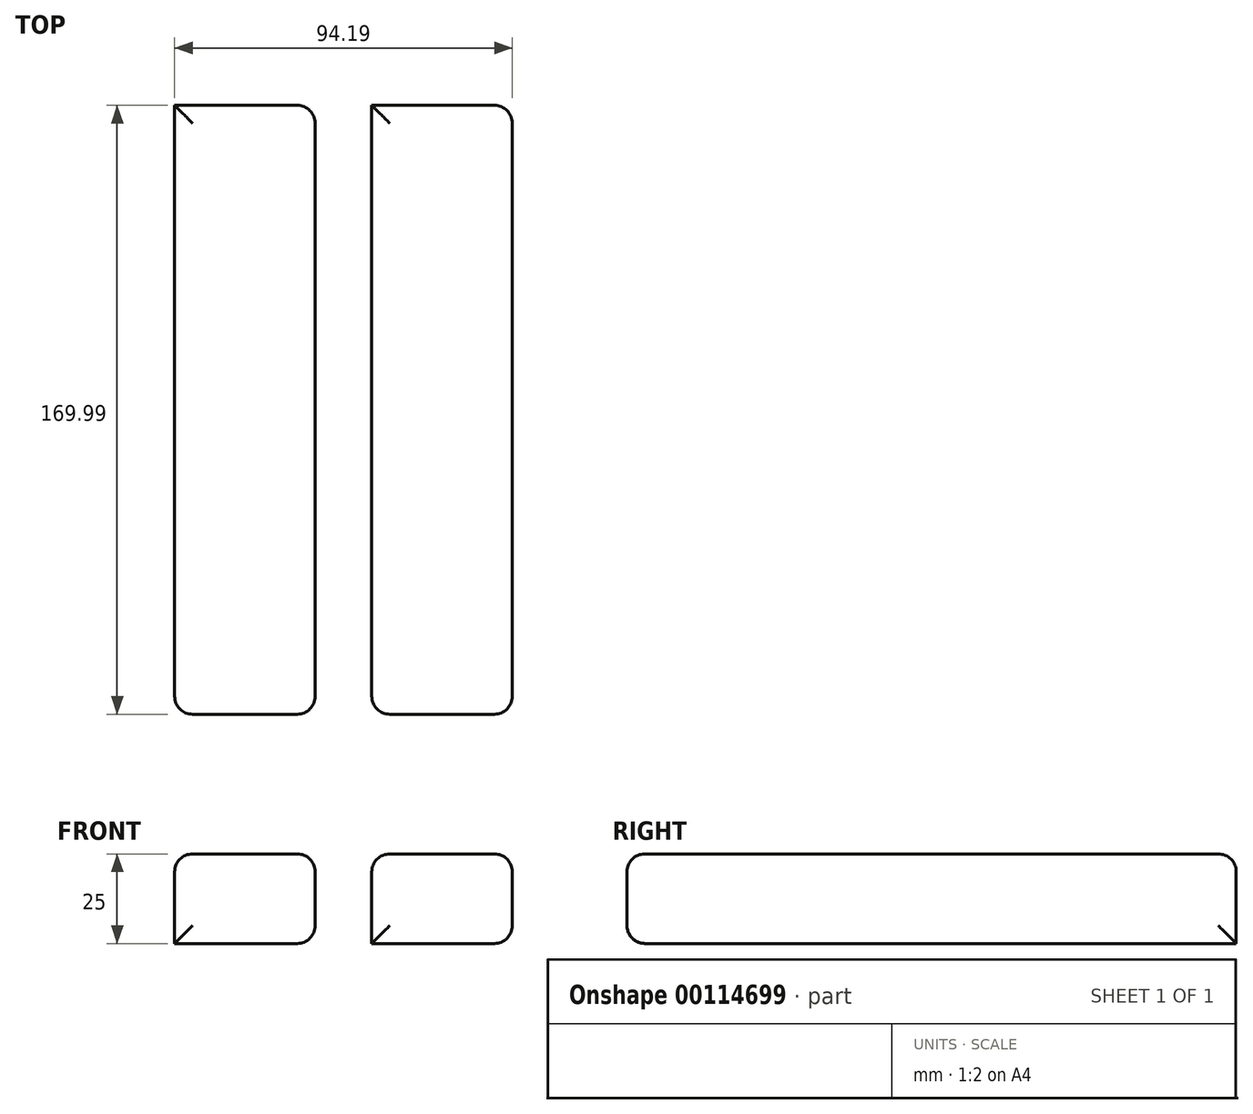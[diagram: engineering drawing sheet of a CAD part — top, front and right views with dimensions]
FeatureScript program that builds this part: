
annotation { "Feature Type Name" : "Feature", "Feature Type Description" : "" }
export const myFeature = defineFeature(function(context is Context, id is Id, definition is map)
    precondition{}
    {
        {
            var Q0;
            Q0=qCreatedBy(makeId("Top.planeOp"),FACE);
            var sketch = newSketch(context, id + "F0", { "sketchPlane" : qUnion([Q0])});
            skLineSegment(sketch, "E0.bottom", {"start": v(39.2, -169.99) * mm, "end": v(0, -169.99) * mm});
            skLineSegment(sketch, "E0.top", {"start": v(39.2, 0) * mm, "end": v(0, 0) * mm});
            skLineSegment(sketch, "E0.left", {"start": v(39.2, -169.99) * mm, "end": v(39.2, 0) * mm});
            skLineSegment(sketch, "E0.right", {"start": v(0, -169.99) * mm, "end": v(0, 0) * mm});
            skSolve(sketch);
        }
        {
            var Q0;
            Q0=makeQuery(id+"F0.imprint","IMPRINT",FACE,{"disambiguationData":[TD([[makeQuery(id+"F0.imprint","IMPRINT",EDGE,{"derivedFrom":sQuery(id+"F0.wireOp",EDGE,"E0.bottom")}),-1.0]])]});
            extrude(context, id + "F1", {"entities" : qUnion([Q0]), "depth" : 25 * mm});
        }
        {
            var Q0;
            Q0=makeQuery(id+"F1.opExtrude","SWEPT_FACE",FACE,{"disambiguationData":[OSD([sQuery(id+"F0.wireOp",EDGE,"E0.left")])]});
            var Q1;
            Q1=makeQuery(id+"F1.opExtrude","SWEPT_FACE",FACE,{"disambiguationData":[OSD([sQuery(id+"F0.wireOp",EDGE,"E0.bottom")])]});
            var Q2;
            Q2=makeQuery(id+"F1.opExtrude","CAP_FACE",FACE,{"disambiguationData":[OSD([sQuery(id+"F0.wireOp",EDGE,"E0.bottom"),sQuery(id+"F0.wireOp",EDGE,"E0.top"),sQuery(id+"F0.wireOp",EDGE,"E0.left"),sQuery(id+"F0.wireOp",EDGE,"E0.right")])],"isStart":false});
            fillet(context, id + "F2", {"entities" : qUnion([Q0, Q1, Q2]), "radius" : 5 * mm, "tangentPropagation" : true, "allowEdgeOverflow" : false});
        }
        {
            var Q0;
            Q0=makeQuery(id+"F1.opExtrude","SWEPT_BODY",BODY,{"disambiguationData":[OSD([sQuery(id+"F0.wireOp",EDGE,"E0.bottom"),sQuery(id+"F0.wireOp",EDGE,"E0.top"),sQuery(id+"F0.wireOp",EDGE,"E0.left"),sQuery(id+"F0.wireOp",EDGE,"E0.right")])]});
            var Q1;
            {var subQ0=sQuery(id+"F0.wireOp",EDGE,"E0.left");Q1=makeQuery(id+"F2.opFillet","BLEND_VERTEX",VERTEX,{"blendedFrom":[makeQuery(id+"F1.opExtrude","SWEPT_EDGE",EDGE,{"disambiguationData":[OSD([sQuery(id+"F0.wireOp",EDGE,"E0.top"),subQ0])]}),makeQuery(id+"F1.opExtrude","CAP_EDGE",EDGE,{"disambiguationData":[OSD([subQ0])],"isStart":true}),makeQuery(id+"F1.opExtrude","SWEPT_FACE",FACE,{"disambiguationData":[OSD([subQ0])]})],"blendedInto":[makeQuery(id+"F1.opExtrude","SWEPT_FACE",FACE,{"disambiguationData":[OSD([subQ0])]})]});}
            var Q2;
            {var subQ0=sQuery(id+"F0.wireOp",EDGE,"E0.right");var subQ1=sQuery(id+"F0.wireOp",EDGE,"E0.top");Q2=makeQuery(id+"F2.opFillet","BLEND_VERTEX",VERTEX,{"blendedFrom":[makeQuery(id+"F1.opExtrude","CAP_EDGE",EDGE,{"disambiguationData":[OSD([subQ1])],"isStart":false}),makeQuery(id+"F1.opExtrude","CAP_EDGE",EDGE,{"disambiguationData":[OSD([subQ0])],"isStart":false}),makeQuery(id+"F1.opExtrude","CAP_FACE",FACE,{"disambiguationData":[OSD([sQuery(id+"F0.wireOp",EDGE,"E0.bottom"),subQ1,sQuery(id+"F0.wireOp",EDGE,"E0.left"),subQ0])],"isStart":false})],"blendedInto":[makeQuery(id+"F1.opExtrude","CAP_FACE",FACE,{"disambiguationData":[OSD([sQuery(id+"F0.wireOp",EDGE,"E0.bottom"),subQ1,sQuery(id+"F0.wireOp",EDGE,"E0.left"),subQ0])],"isStart":false})]});}
            transform(context, id + "F3", {"entities" : qUnion([Q0]), "transformType" : TransformType.TRANSLATION_3D, "dx" : 55 * mm, "dy" : 0 * mm, "dz" : 0 * mm, "makeCopy" : true});
        }
    });
